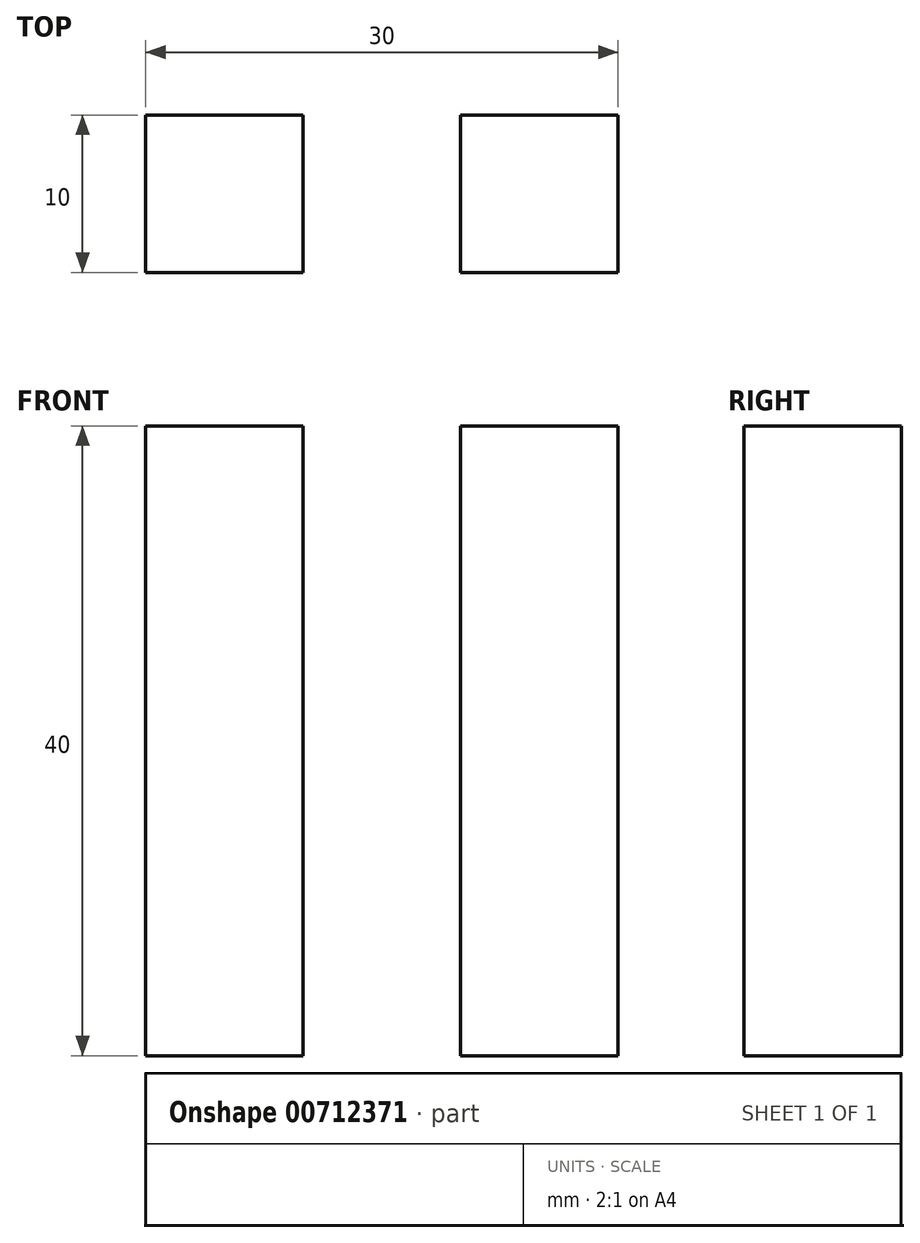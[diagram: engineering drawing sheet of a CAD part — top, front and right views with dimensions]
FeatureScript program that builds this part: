
annotation { "Feature Type Name" : "Feature", "Feature Type Description" : "" }
export const myFeature = defineFeature(function(context is Context, id is Id, definition is map)
    precondition{}
    {
        {
            var Q0;
            Q0=qCreatedBy(makeId("Top.planeOp"),FACE);
            var sketch = newSketch(context, id + "F0", { "sketchPlane" : qUnion([Q0])});
            skLineSegment(sketch, "E0.bottom", {"start": v(0, 0) * mm, "end": v(10, 0) * mm});
            skLineSegment(sketch, "E0.top", {"start": v(0, 10) * mm, "end": v(10, 10) * mm});
            skLineSegment(sketch, "E0.left", {"start": v(0, 0) * mm, "end": v(0, 10) * mm});
            skLineSegment(sketch, "E0.right", {"start": v(10, 0) * mm, "end": v(10, 10) * mm});
            skLineSegment(sketch, "E1.bottom", {"start": v(20, 0) * mm, "end": v(30, 0) * mm});
            skLineSegment(sketch, "E1.top", {"start": v(20, 10) * mm, "end": v(30, 10) * mm});
            skLineSegment(sketch, "E1.left", {"start": v(20, 0) * mm, "end": v(20, 10) * mm});
            skLineSegment(sketch, "E1.right", {"start": v(30, 0) * mm, "end": v(30, 10) * mm});
            skSolve(sketch);
        }
        {
            var Q0;
            Q0 = qSketchRegion(id + "F0", true);
            extrude(context, id + "F1", {"entities" : qUnion([Q0]), "depth" : 40 * mm, "offsetDistance" : 25.4 * mm});
        }
    });
